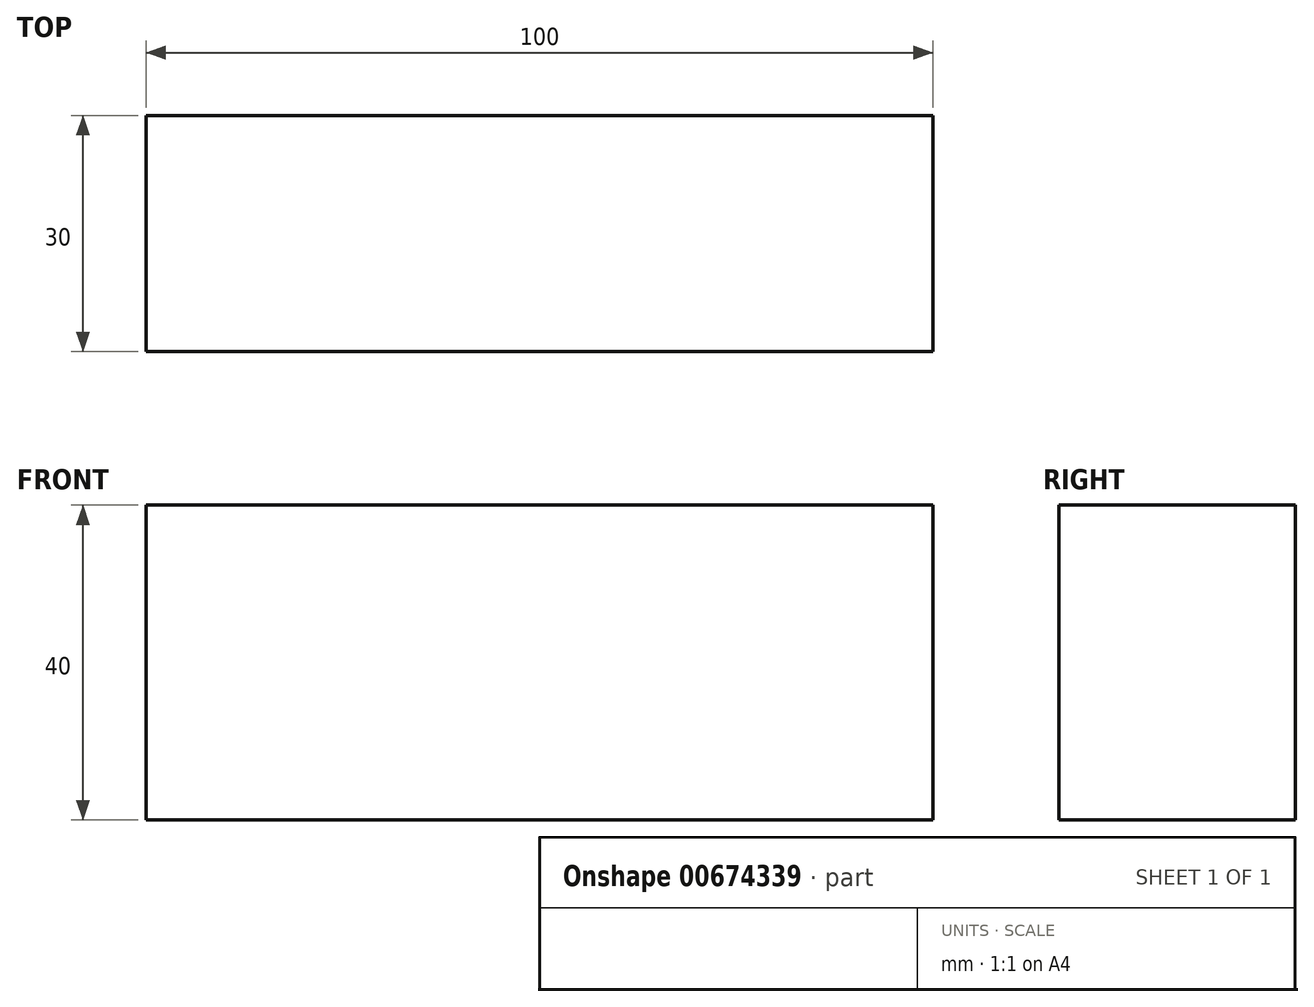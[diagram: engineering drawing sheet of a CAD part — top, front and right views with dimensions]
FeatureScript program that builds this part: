
annotation { "Feature Type Name" : "Feature", "Feature Type Description" : "" }
export const myFeature = defineFeature(function(context is Context, id is Id, definition is map)
    precondition{}
    {
        {
            var Q0;
            Q0=qCreatedBy(makeId("Top.planeOp"),FACE);
            var sketch = newSketch(context, id + "F0", { "sketchPlane" : qUnion([Q0])});
            skLineSegment(sketch, "E0.bottom", {"start": v(50, -15) * mm, "end": v(-50, -15) * mm});
            skLineSegment(sketch, "E0.top", {"start": v(50, 15) * mm, "end": v(-50, 15) * mm});
            skLineSegment(sketch, "E0.left", {"start": v(50, -15) * mm, "end": v(50, 15) * mm});
            skLineSegment(sketch, "E0.right", {"start": v(-50, -15) * mm, "end": v(-50, 15) * mm});
            skPoint(sketch, "E0.middle", {"position": v(0, 0) * mm});
            skSolve(sketch);
        }
        {
            var Q0;
            Q0=makeQuery(id+"F0.imprint","IMPRINT",FACE,{"disambiguationData":[TD([[makeQuery(id+"F0.imprint","IMPRINT",EDGE,{"derivedFrom":sQuery(id+"F0.wireOp",EDGE,"E0.bottom")}),-1.0]])]});
            extrude(context, id + "F1", {"entities" : qUnion([Q0]), "oppositeDirection" : true, "depth" : 40 * mm, "offsetDistance" : 25 * mm});
        }
    });
